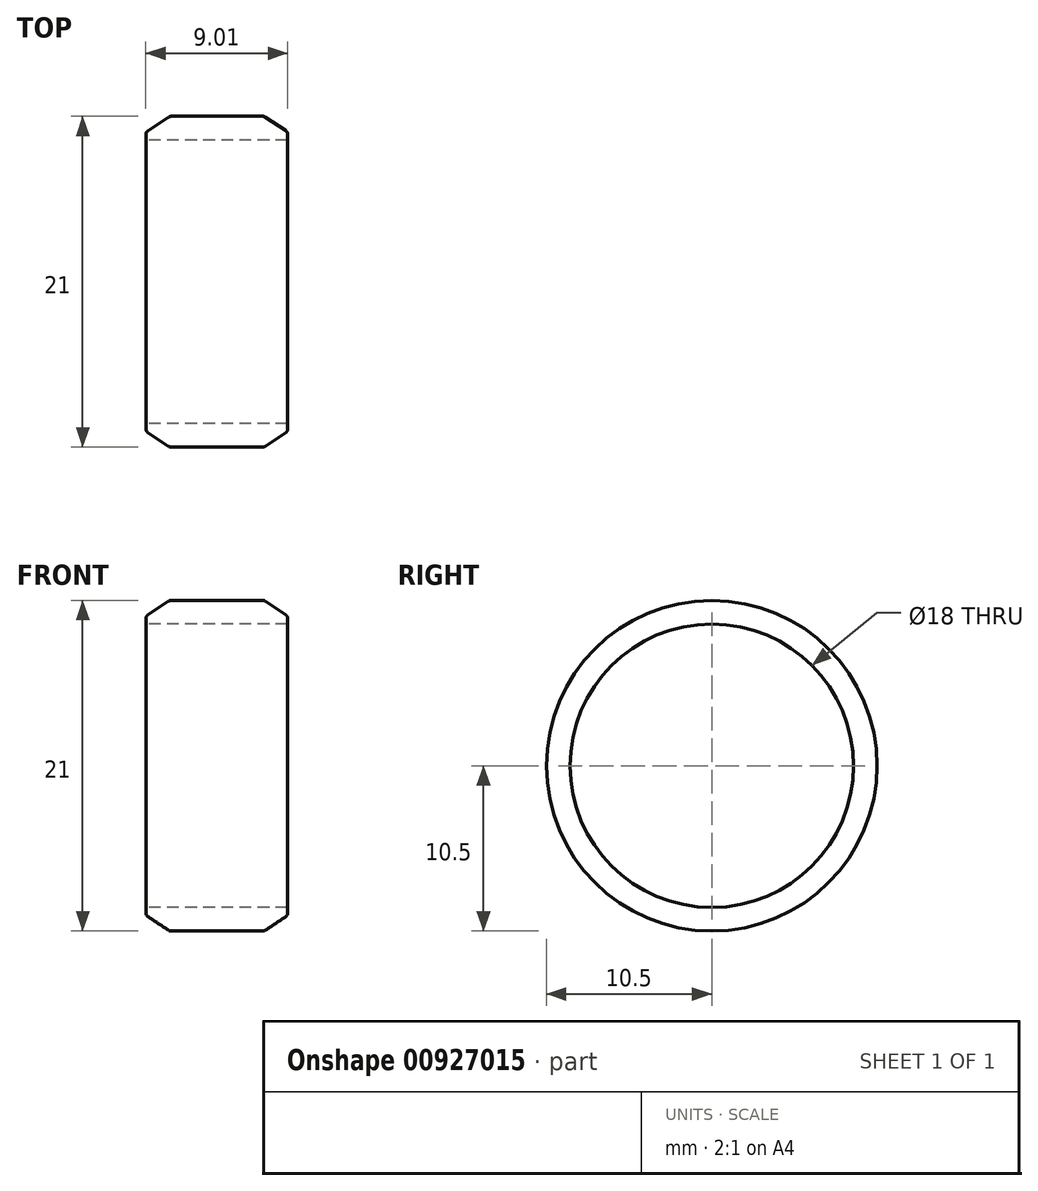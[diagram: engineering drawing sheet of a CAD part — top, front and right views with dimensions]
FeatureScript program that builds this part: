
annotation { "Feature Type Name" : "Feature", "Feature Type Description" : "" }
export const myFeature = defineFeature(function(context is Context, id is Id, definition is map)
    precondition{}
    {
        {
            var Q0;
            Q0=qCreatedBy(makeId("Front.planeOp"),FACE);
            var sketch = newSketch(context, id + "F0", { "sketchPlane" : qUnion([Q0])});
            skLineSegment(sketch, "E0", {"start": v(-71.92, 0) * mm, "end": v(65.43, 0) * mm});
            skSolve(sketch);
        }
        {
            var Q0;
            Q0=qCreatedBy(makeId("Front.planeOp"),FACE);
            var sketch = newSketch(context, id + "F1", { "sketchPlane" : qUnion([Q0])});
            skLineSegment(sketch, "E1", {"start": v(-4.5, 9.5) * mm, "end": v(4.5, 9.5) * mm, "construction": true});
            skLineSegment(sketch, "E2", {"start": v(-3, 10.5) * mm, "end": v(3, 10.5) * mm});
            skLineSegment(sketch, "E3", {"start": v(3, 10.5) * mm, "end": v(4.5, 9.5) * mm});
            skLineSegment(sketch, "E4", {"start": v(-3, 10.5) * mm, "end": v(-4.5, 9.5) * mm});
            skLineSegment(sketch, "E5", {"start": v(-4.52, 9) * mm, "end": v(4.48, 9) * mm});
            skLineSegment(sketch, "E6", {"start": v(-4.5, 9.5) * mm, "end": v(-4.52, 9) * mm});
            skLineSegment(sketch, "E7", {"start": v(4.5, 9.5) * mm, "end": v(4.48, 9) * mm});
            skSolve(sketch);
        }
        {
            var Q0;
            Q0=makeQuery(id+"F1.imprint","IMPRINT",FACE,{"disambiguationData":[TD([[makeQuery(id+"F1.imprint","IMPRINT",EDGE,{"derivedFrom":sQuery(id+"F1.wireOp",EDGE,"E1")}),1.0]])]});
            var Q1;
            Q1=makeQuery(id+"F1.imprint","IMPRINT",FACE,{"disambiguationData":[TD([[makeQuery(id+"F1.imprint","IMPRINT",EDGE,{"derivedFrom":sQuery(id+"F1.wireOp",EDGE,"E2")}),-1.0]])]});
            var Q2;
            Q2=sQuery(id+"F1.wireOp",EDGE,"E2");
            var Q3;
            Q3=sQuery(id+"F1.wireOp",EDGE,"E4");
            var Q4;
            Q4=sQuery(id+"F1.wireOp",EDGE,"E1");
            var Q5;
            Q5=sQuery(id+"F1.wireOp",EDGE,"E3");
            var Q6;
            Q6=sQuery(id+"F0.wireOp",EDGE,"E0");
            revolve(context, id + "F2", {"surfaceOperationType" : NewSurfaceOperationType.NEW, "entities" : qUnion([Q0, Q1]), "surfaceEntities" : qUnion([Q2, Q3, Q4, Q5]), "axis" : qUnion([Q6]), "revolveType" : RevolveType.FULL});
        }
        {
            var Q0;
            Q0=makeQuery(id+"F2.opRevolve","SWEPT_EDGE",EDGE,{"disambiguationData":[OSD([sQuery(id+"F1.wireOp",EDGE,"E3"),sQuery(id+"F1.wireOp",EDGE,"E7")])]});
            var Q1;
            Q1=makeQuery(id+"F2.opRevolve","SWEPT_EDGE",EDGE,{"disambiguationData":[OSD([sQuery(id+"F1.wireOp",EDGE,"E4"),sQuery(id+"F1.wireOp",EDGE,"E6")])]});
            var Q2;
            Q2=makeQuery(id+"F2.opRevolve","SWEPT_EDGE",EDGE,{"disambiguationData":[OSD([sQuery(id+"F1.wireOp",EDGE,"E2"),sQuery(id+"F1.wireOp",EDGE,"E4")])]});
            var Q3;
            Q3=makeQuery(id+"F2.opRevolve","SWEPT_EDGE",EDGE,{"disambiguationData":[OSD([sQuery(id+"F1.wireOp",EDGE,"E2"),sQuery(id+"F1.wireOp",EDGE,"E3")])]});
            fillet(context, id + "F3", {"entities" : qUnion([Q0, Q1, Q2, Q3]), "radius" : 0.25 * mm, "tangentPropagation" : true, "allowEdgeOverflow" : false});
        }
    });
